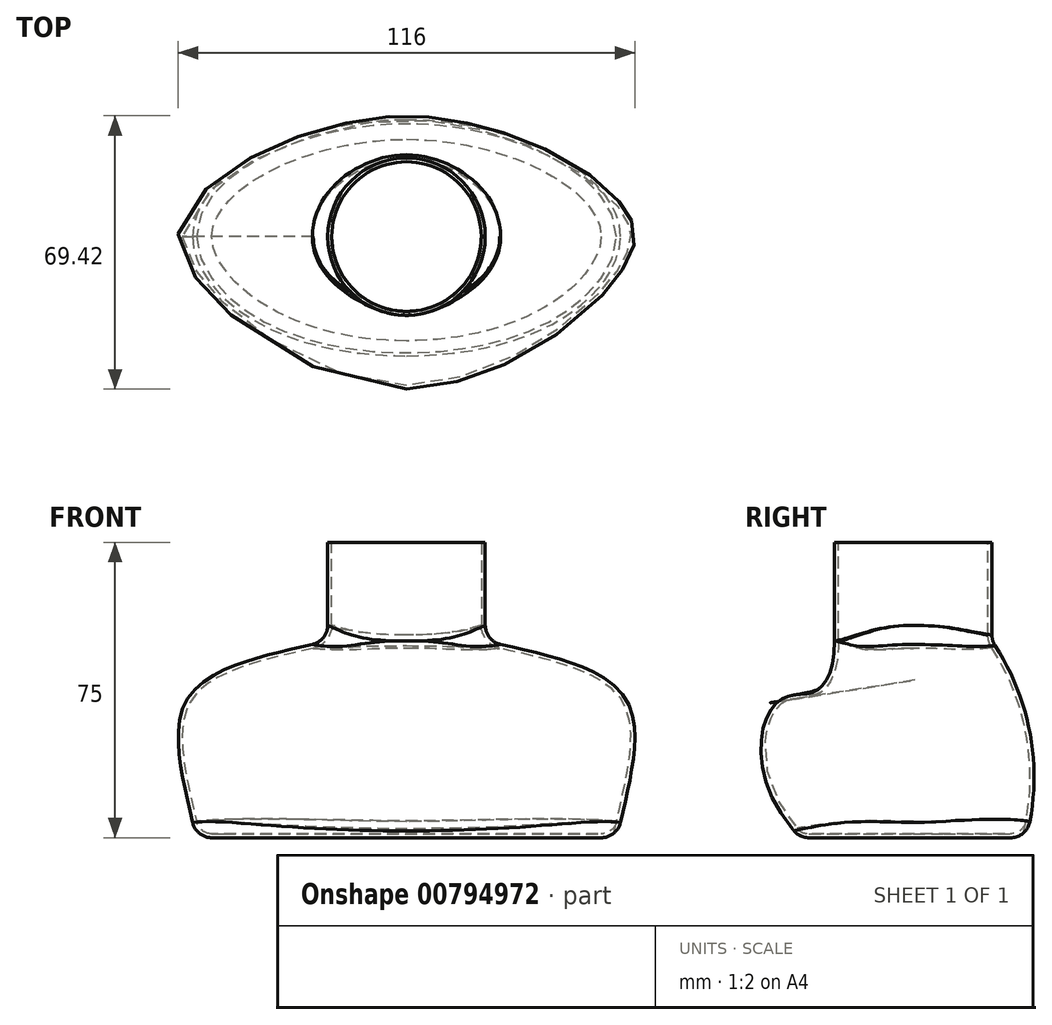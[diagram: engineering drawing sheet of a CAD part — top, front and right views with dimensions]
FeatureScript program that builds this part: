
annotation { "Feature Type Name" : "Feature", "Feature Type Description" : "" }
export const myFeature = defineFeature(function(context is Context, id is Id, definition is map)
    precondition{}
    {
        {
            var Q0;
            Q0=qCreatedBy(makeId("Top.planeOp"),FACE);
            var sketch = newSketch(context, id + "F0", { "sketchPlane" : qUnion([Q0])});
            skEllipse(sketch, "E0", {"center": v(0, 0) * mm, "majorRadius": 53.49 * mm, "minorRadius": 28.71 * mm, "majorAxis": v(1, 0)});
            skSolve(sketch);
        }
        {
            var Q0;
            Q0=qCreatedBy(makeId("Top.planeOp"),FACE);
            cPlane(context, id + "F1", {"entities" : qUnion([Q0]), "cplaneType" : CPlaneType.OFFSET, "offset" : 50 * mm, "width" : 150 * mm, "height" : 150 * mm});
        }
        {
            var Q0;
            Q0=qCreatedBy(id+"F1.planeOp",FACE);
            var sketch = newSketch(context, id + "F2", { "sketchPlane" : qUnion([Q0])});
            skCircle(sketch, "E1", {"center": v(0, 0) * mm, "radius": 20 * mm});
            skSolve(sketch);
        }
        {
            var Q0;
            Q0=qCreatedBy(makeId("Right.planeOp"),FACE);
            var sketch = newSketch(context, id + "F3", { "sketchPlane" : qUnion([Q0])});
            skFitSpline(sketch, "E2", {"points": [v(-28.71, 0) * mm, v(-34.15, 34.8) * mm, v(-25.66, 36.92) * mm, v(-20, 50) * mm], "startDerivative": vector(-89.8, 94.5) * mm, "endDerivative": vector(-0.65, 80.14) * mm});
            skArc(sketch, "E3", {"start": v(28.71, 0) * mm, "mid": v(29.78, 25.95) * mm, "end": v(20, 50) * mm});
            skSolve(sketch);
        }
        {
            var Q0;
            Q0=qCreatedBy(makeId("Front.planeOp"),FACE);
            var sketch = newSketch(context, id + "F4", { "sketchPlane" : qUnion([Q0])});
            skFitSpline(sketch, "E4", {"points": [v(-53.49, 0) * mm, v(-55.61, 35.35) * mm, v(-20, 50) * mm], "startDerivative": vector(-17.3, 81.79) * mm, "endDerivative": vector(83.82, 19.44) * mm});
            skFitSpline(sketch, "E5.MirrorCS", {"points": [v(53.49, 0) * mm, v(55.61, 35.35) * mm, v(20, 50) * mm], "startDerivative": vector(17.3, 81.79) * mm, "endDerivative": vector(-83.82, 19.44) * mm});
            skSolve(sketch);
        }
        {
            var Q0;
            Q0=makeQuery(id+"F2.imprint","IMPRINT",FACE,{"disambiguationData":[TD([[makeQuery(id+"F2.imprint","IMPRINT",EDGE,{"derivedFrom":sQuery(id+"F2.wireOp",EDGE,"E1")}),1.0]])]});
            var Q1;
            Q1=makeQuery(id+"F0.imprint","IMPRINT",FACE,{"disambiguationData":[TD([[makeQuery(id+"F0.imprint","IMPRINT",EDGE,{"derivedFrom":sQuery(id+"F0.wireOp",EDGE,"E0")}),1.0]])]});
            var Q2;
            Q2=sQuery(id+"F4.wireOp",EDGE,"E4");
            var Q3;
            Q3=sQuery(id+"F4.wireOp",EDGE,"E5.MirrorCS");
            var Q4;
            Q4=sQuery(id+"F3.wireOp",EDGE,"E3");
            var Q5;
            Q5=sQuery(id+"F3.wireOp",EDGE,"E2");
            loft(context, id + "F5", {"addGuides" : true, "sheetProfilesArray" : [{ "sheetProfileEntities" : qUnion([Q0]) }, { "sheetProfileEntities" : qUnion([Q1]) }], "guidesArray" : [{ "guideEntities" : qUnion([Q2]), "guideDerivativeType" : LoftGuideDerivativeType.DEFAULT, "guideDerivativeMagnitude" : 1 }, { "guideEntities" : qUnion([Q3]), "guideDerivativeType" : LoftGuideDerivativeType.DEFAULT, "guideDerivativeMagnitude" : 1 }, { "guideEntities" : qUnion([Q4]), "guideDerivativeType" : LoftGuideDerivativeType.DEFAULT, "guideDerivativeMagnitude" : 1 }, { "guideEntities" : qUnion([Q5]), "guideDerivativeType" : LoftGuideDerivativeType.DEFAULT, "guideDerivativeMagnitude" : 1 }]});
        }
        {
            var Q0;
            Q0=makeQuery(id+"F5.opLoft","CAP_FACE",FACE,{"disambiguationData":[OSD([makeQuery(id+"F2.imprint","IMPRINT",FACE,{"disambiguationData":[TD([[makeQuery(id+"F2.imprint","IMPRINT",EDGE,{"derivedFrom":sQuery(id+"F2.wireOp",EDGE,"E1")}),1.0]])]})])],"isStart":true});
            extrude(context, id + "F6", {"entities" : qUnion([Q0]), "operationType" : NewBodyOperationType.ADD, "depth" : 25 * mm, "offsetDistance" : 25 * mm});
        }
        {
            var Q0;
            {var subQ0=sQuery(id+"F4.wireOp",EDGE,"E5.MirrorCS");var subQ1=sQuery(id+"F3.wireOp",EDGE,"E2");var subQ2=sQuery(id+"F2.wireOp",EDGE,"E1");Q0=makeQuery(id+"F6.boolean.opBoolean","MERGE",EDGE,{"derivedFrom":[makeQuery(id+"F5.opLoft","MID_CAP_EDGE",EDGE,{"disambiguationData":[OSD([subQ2,subQ1,subQ0])],"capPos":0.0}),makeQuery(id+"F6.opExtrude","CAP_EDGE",EDGE,{"disambiguationData":[OSD([subQ2,subQ1,subQ0])],"isStart":true})]});}
            fillet(context, id + "F7", {"entities" : qUnion([Q0]), "radius" : 5 * mm, "tangentPropagation" : true, "allowEdgeOverflow" : false});
        }
        {
            var Q0;
            Q0=makeQuery(id+"F5.opLoft","MID_CAP_EDGE",EDGE,{"disambiguationData":[OSD([sQuery(id+"F0.wireOp",EDGE,"E0"),sQuery(id+"F3.wireOp",EDGE,"E2"),sQuery(id+"F4.wireOp",EDGE,"E4")])],"capPos":1.0});
            fillet(context, id + "F8", {"entities" : qUnion([Q0]), "radius" : 5 * mm, "tangentPropagation" : true, "allowEdgeOverflow" : false});
        }
        {
            var Q0;
            Q0=makeQuery(id+"F6.opExtrude","CAP_FACE",FACE,{"disambiguationData":[OSD([makeQuery(id+"F2.imprint","IMPRINT",FACE,{"disambiguationData":[TD([[makeQuery(id+"F2.imprint","IMPRINT",EDGE,{"derivedFrom":sQuery(id+"F2.wireOp",EDGE,"E1")}),1.0]])]})])],"isStart":false});
            shell(context, id + "F9", {"entities" : qUnion([Q0]), "thickness" : 1 * mm});
        }
    });
